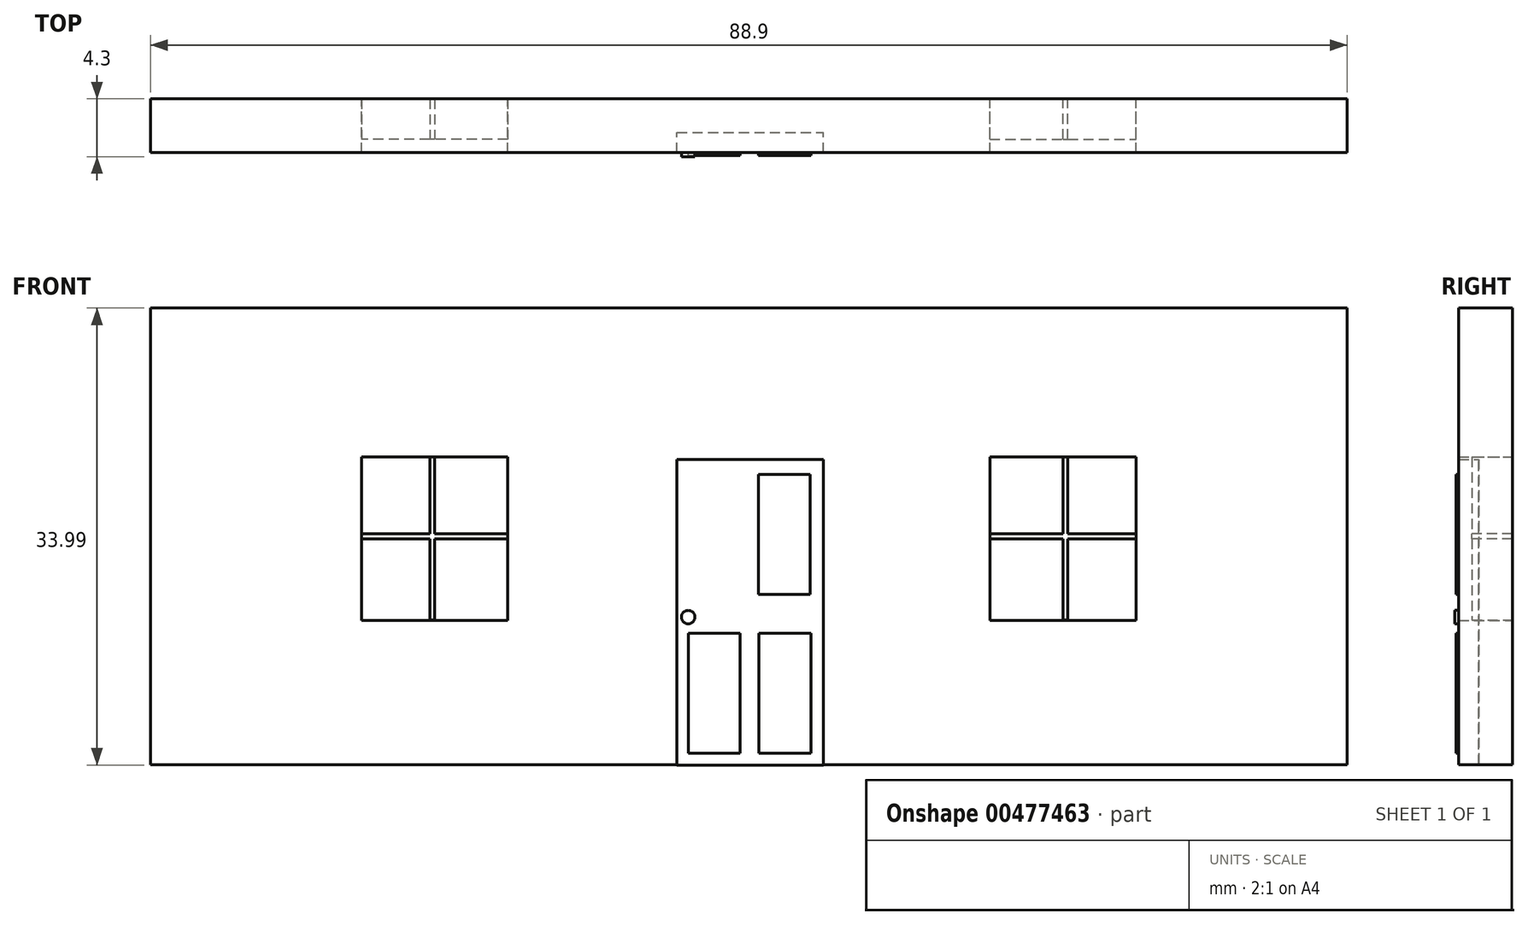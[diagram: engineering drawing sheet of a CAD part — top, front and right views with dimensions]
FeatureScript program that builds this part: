
annotation { "Feature Type Name" : "Feature", "Feature Type Description" : "" }
export const myFeature = defineFeature(function(context is Context, id is Id, definition is map)
    precondition{}
    {
        {
            var Q0;
            Q0=qCreatedBy(makeId("Front.planeOp"),FACE);
            var sketch = newSketch(context, id + "F0", { "sketchPlane" : qUnion([Q0])});
            skLineSegment(sketch, "E0.bottom", {"start": v(-44.45, 17) * mm, "end": v(44.45, 17) * mm});
            skLineSegment(sketch, "E0.top", {"start": v(-44.45, -17) * mm, "end": v(44.45, -17) * mm});
            skLineSegment(sketch, "E0.left", {"start": v(-44.45, 17) * mm, "end": v(-44.45, -17) * mm});
            skLineSegment(sketch, "E0.right", {"start": v(44.45, 17) * mm, "end": v(44.45, -17) * mm});
            skPoint(sketch, "E0.middle", {"position": v(0, 0) * mm});
            skLineSegment(sketch, "E1.bottom", {"start": v(-5.34, -17) * mm, "end": v(5.54, -17) * mm});
            skLineSegment(sketch, "E1.top", {"start": v(-5.34, 5.74) * mm, "end": v(5.54, 5.74) * mm});
            skLineSegment(sketch, "E1.left", {"start": v(-5.34, -17) * mm, "end": v(-5.34, 5.74) * mm});
            skLineSegment(sketch, "E1.right", {"start": v(5.54, -17) * mm, "end": v(5.54, 5.74) * mm});
            skLineSegment(sketch, "E2.bottom", {"start": v(17.91, -6.26) * mm, "end": v(28.8, -6.26) * mm});
            skLineSegment(sketch, "E2.top", {"start": v(17.91, 5.9) * mm, "end": v(28.8, 5.9) * mm});
            skLineSegment(sketch, "E2.left", {"start": v(17.91, -6.26) * mm, "end": v(17.91, 5.9) * mm});
            skLineSegment(sketch, "E2.right", {"start": v(28.8, -6.26) * mm, "end": v(28.8, 5.9) * mm});
            skLineSegment(sketch, "E3.MirrorCS", {"start": v(-17.91, -6.26) * mm, "end": v(-28.8, -6.26) * mm});
            skLineSegment(sketch, "E4.MirrorCS", {"start": v(-17.91, -6.26) * mm, "end": v(-17.91, 5.9) * mm});
            skLineSegment(sketch, "E5.MirrorCS", {"start": v(-28.8, -6.26) * mm, "end": v(-28.8, 5.9) * mm});
            skLineSegment(sketch, "E6.MirrorCS", {"start": v(-17.91, 5.9) * mm, "end": v(-28.8, 5.9) * mm});
            skSolve(sketch);
        }
        {
            var Q0;
            Q0=makeQuery(id+"F0.imprint","IMPRINT",FACE,{"disambiguationData":[TD([[makeQuery(id+"F0.imprint","IMPRINT",EDGE,{"derivedFrom":sQuery(id+"F0.wireOp",EDGE,"E0.bottom")}),-1.0]])]});
            extrude(context, id + "F1", {"entities" : qUnion([Q0]), "depth" : 4 * mm});
        }
        {
            var Q0;
            Q0=qCreatedBy(makeId("Front.planeOp"),FACE);
            var sketch = newSketch(context, id + "F2", { "sketchPlane" : qUnion([Q0])});
            skLineSegment(sketch, "E7.bottom", {"start": v(-23.36, 6.23) * mm, "end": v(-23.71, 6.23) * mm});
            skLineSegment(sketch, "E7.top", {"start": v(-23.36, -6.23) * mm, "end": v(-23.71, -6.23) * mm});
            skLineSegment(sketch, "E7.left", {"start": v(-23.36, 6.23) * mm, "end": v(-23.36, -6.23) * mm});
            skLineSegment(sketch, "E7.right", {"start": v(-23.71, 6.23) * mm, "end": v(-23.71, -6.23) * mm});
            skPoint(sketch, "E7.middle", {"position": v(-23.54, 0) * mm});
            skLineSegment(sketch, "E8.bottom", {"start": v(-17.33, 0.18) * mm, "end": v(-29.74, 0.18) * mm});
            skLineSegment(sketch, "E8.top", {"start": v(-17.33, -0.18) * mm, "end": v(-29.74, -0.18) * mm});
            skLineSegment(sketch, "E8.left", {"start": v(-17.33, 0.18) * mm, "end": v(-17.33, -0.18) * mm});
            skLineSegment(sketch, "E8.right", {"start": v(-29.74, 0.18) * mm, "end": v(-29.74, -0.18) * mm});
            skLineSegment(sketch, "E9.MirrorCS", {"start": v(29.74, 0.18) * mm, "end": v(29.74, -0.18) * mm});
            skLineSegment(sketch, "E10.MirrorCS", {"start": v(17.33, 0.18) * mm, "end": v(17.33, -0.18) * mm});
            skLineSegment(sketch, "E11.MirrorCS", {"start": v(17.33, 0.18) * mm, "end": v(29.74, 0.18) * mm});
            skLineSegment(sketch, "E12.MirrorCS", {"start": v(17.33, -0.18) * mm, "end": v(29.74, -0.18) * mm});
            skLineSegment(sketch, "E13.MirrorCS", {"start": v(23.36, 6.23) * mm, "end": v(23.71, 6.23) * mm});
            skLineSegment(sketch, "E14.MirrorCS", {"start": v(23.36, -6.23) * mm, "end": v(23.71, -6.23) * mm});
            skLineSegment(sketch, "E15.MirrorCS", {"start": v(23.71, 6.23) * mm, "end": v(23.71, -6.23) * mm});
            skLineSegment(sketch, "E16.MirrorCS", {"start": v(23.36, 6.23) * mm, "end": v(23.36, -6.23) * mm});
            skPoint(sketch, "E17.MirrorP", {"position": v(23.54, 0) * mm});
            skSolve(sketch);
        }
        {
            var Q0;
            Q0 = qSketchRegion(id + "F2", true);
            extrude(context, id + "F3", {"entities" : qUnion([Q0]), "operationType" : NewBodyOperationType.ADD, "depth" : 3 * mm});
        }
        {
            var Q0;
            Q0=qCreatedBy(makeId("Front.planeOp"),FACE);
            var sketch = newSketch(context, id + "F4", { "sketchPlane" : qUnion([Q0])});
            skLineSegment(sketch, "E18.bottom", {"start": v(-5.34, 5.75) * mm, "end": v(5.56, 5.75) * mm});
            skLineSegment(sketch, "E18.top", {"start": v(-5.34, -17) * mm, "end": v(5.56, -17) * mm});
            skLineSegment(sketch, "E18.left", {"start": v(-5.34, 5.75) * mm, "end": v(-5.34, -17) * mm});
            skLineSegment(sketch, "E18.right", {"start": v(5.56, 5.75) * mm, "end": v(5.56, -17) * mm});
            skSolve(sketch);
        }
        {
            var Q0;
            Q0 = qSketchRegion(id + "F4", true);
            extrude(context, id + "F5", {"entities" : qUnion([Q0]), "operationType" : NewBodyOperationType.ADD, "depth" : 2.5 * mm});
        }
        {
            var Q0;
            Q0=makeQuery(id+"F1.opExtrude","CAP_FACE",FACE,{"disambiguationData":[OSD([sQuery(id+"F0.wireOp",EDGE,"E0.bottom"),sQuery(id+"F0.wireOp",EDGE,"E0.top"),sQuery(id+"F0.wireOp",EDGE,"E0.left"),sQuery(id+"F0.wireOp",EDGE,"E0.right"),sQuery(id+"F0.wireOp",EDGE,"E1.top"),sQuery(id+"F0.wireOp",EDGE,"E1.left"),sQuery(id+"F0.wireOp",EDGE,"E1.right"),sQuery(id+"F0.wireOp",EDGE,"E2.bottom"),sQuery(id+"F0.wireOp",EDGE,"E2.top"),sQuery(id+"F0.wireOp",EDGE,"E2.left"),sQuery(id+"F0.wireOp",EDGE,"E2.right"),sQuery(id+"F0.wireOp",EDGE,"E3.MirrorCS"),sQuery(id+"F0.wireOp",EDGE,"E4.MirrorCS"),sQuery(id+"F0.wireOp",EDGE,"E5.MirrorCS"),sQuery(id+"F0.wireOp",EDGE,"E6.MirrorCS")])],"isStart":false});
            var sketch = newSketch(context, id + "F6", { "sketchPlane" : qUnion([Q0])});
            skLineSegment(sketch, "E19.bottom", {"start": v(-4.56, 4.62) * mm, "end": v(-0.7, 4.62) * mm});
            skLineSegment(sketch, "E19.top", {"start": v(-4.56, -4.3) * mm, "end": v(-0.7, -4.3) * mm});
            skLineSegment(sketch, "E19.left", {"start": v(-4.56, 4.62) * mm, "end": v(-4.56, -4.3) * mm});
            skLineSegment(sketch, "E19.right", {"start": v(-0.7, 4.62) * mm, "end": v(-0.7, -4.3) * mm});
            skLineSegment(sketch, "E20.MirrorCS", {"start": v(4.56, 4.62) * mm, "end": v(4.56, -4.3) * mm});
            skLineSegment(sketch, "E21.MirrorCS", {"start": v(4.56, -4.3) * mm, "end": v(0.7, -4.3) * mm});
            skLineSegment(sketch, "E22.MirrorCS", {"start": v(0.7, 4.62) * mm, "end": v(0.7, -4.3) * mm});
            skLineSegment(sketch, "E23.MirrorCS", {"start": v(4.56, 4.62) * mm, "end": v(0.7, 4.62) * mm});
            skLineSegment(sketch, "E24.MirrorCS", {"start": v(-4.5, -16.12) * mm, "end": v(-4.5, -7.2) * mm});
            skLineSegment(sketch, "E25.MirrorCS", {"start": v(4.61, -16.12) * mm, "end": v(4.61, -7.2) * mm});
            skLineSegment(sketch, "E26.MirrorCS", {"start": v(0.75, -16.12) * mm, "end": v(0.75, -7.2) * mm});
            skLineSegment(sketch, "E27.MirrorCS", {"start": v(-4.5, -7.2) * mm, "end": v(-0.65, -7.2) * mm});
            skLineSegment(sketch, "E28.MirrorCS", {"start": v(4.61, -16.12) * mm, "end": v(0.75, -16.12) * mm});
            skLineSegment(sketch, "E29.MirrorCS", {"start": v(-0.65, -16.12) * mm, "end": v(-0.65, -7.2) * mm});
            skLineSegment(sketch, "E30.MirrorCS", {"start": v(-4.5, -16.12) * mm, "end": v(-0.65, -16.12) * mm});
            skLineSegment(sketch, "E31.MirrorCS", {"start": v(4.61, -7.2) * mm, "end": v(0.75, -7.2) * mm});
            skCircle(sketch, "E32", {"center": v(-4.5, -6) * mm, "radius": 0.5 * mm});
            skSolve(sketch);
        }
        {
            var Q0;
            Q0=makeQuery(id+"F6.imprint","IMPRINT",FACE,{"disambiguationData":[TD([[makeQuery(id+"F6.imprint","IMPRINT",EDGE,{"derivedFrom":sQuery(id+"F6.wireOp",EDGE,"E19.left")}),1.0]])]});
            var Q1;
            Q1=makeQuery(id+"F6.imprint","IMPRINT",FACE,{"disambiguationData":[TD([[makeQuery(id+"F6.imprint","IMPRINT",EDGE,{"derivedFrom":sQuery(id+"F6.wireOp",EDGE,"E23.MirrorCS")}),1.0]])]});
            var Q2;
            Q2=makeQuery(id+"F6.imprint","IMPRINT",FACE,{"disambiguationData":[TD([[makeQuery(id+"F6.imprint","IMPRINT",EDGE,{"derivedFrom":sQuery(id+"F6.wireOp",EDGE,"E25.MirrorCS")}),1.0]])]});
            var Q3;
            Q3=makeQuery(id+"F6.imprint","IMPRINT",FACE,{"disambiguationData":[TD([[makeQuery(id+"F6.imprint","IMPRINT",EDGE,{"derivedFrom":sQuery(id+"F6.wireOp",EDGE,"E24.MirrorCS")}),-1.0]])]});
            extrude(context, id + "F7", {"entities" : qUnion([Q0, Q1, Q2, Q3]), "depth" : .2 * mm});
        }
        {
            var Q0;
            Q0=makeQuery(id+"F6.imprint","IMPRINT",FACE,{"disambiguationData":[TD([[makeQuery(id+"F6.imprint","IMPRINT",EDGE,{"derivedFrom":sQuery(id+"F6.wireOp",EDGE,"E32")}),1.0]])]});
            extrude(context, id + "F8", {"entities" : qUnion([Q0]), "depth" : .3 * mm});
        }
    });
